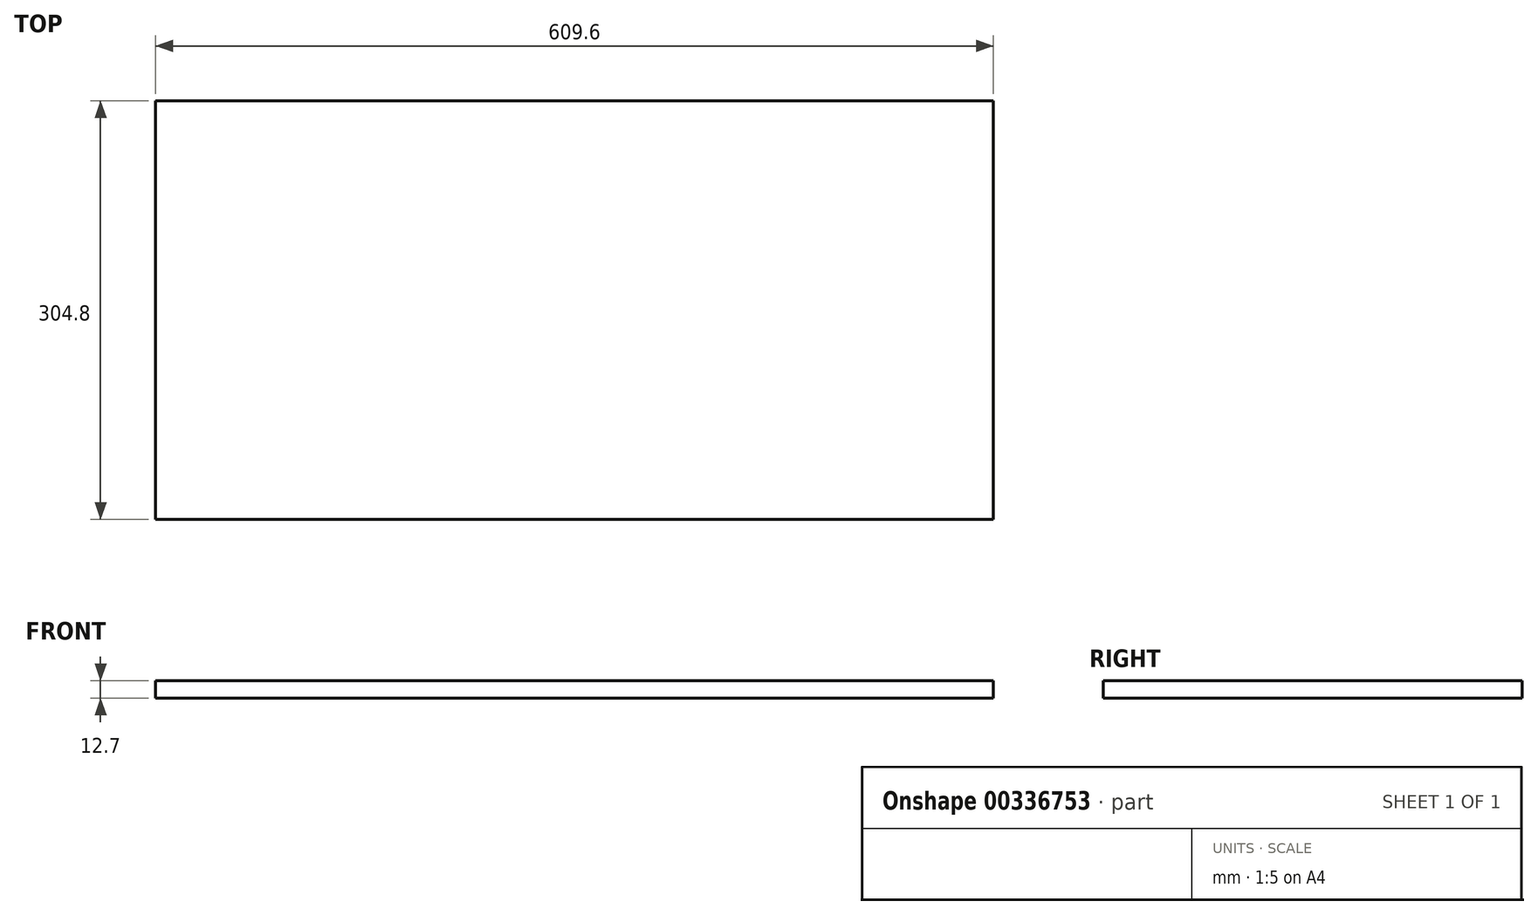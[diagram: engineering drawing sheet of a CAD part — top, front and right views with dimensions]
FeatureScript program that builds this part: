
annotation { "Feature Type Name" : "Feature", "Feature Type Description" : "" }
export const myFeature = defineFeature(function(context is Context, id is Id, definition is map)
    precondition{}
    {
        {
            var Q0;
            Q0=qCreatedBy(makeId("Top.planeOp"),FACE);
            var sketch = newSketch(context, id + "F0", { "sketchPlane" : qUnion([Q0])});
            skLineSegment(sketch, "E0.bottom", {"start": v(0, 0) * mm, "end": v(609.6, 0) * mm});
            skLineSegment(sketch, "E0.top", {"start": v(0, -304.8) * mm, "end": v(609.6, -304.8) * mm});
            skLineSegment(sketch, "E0.left", {"start": v(0, 0) * mm, "end": v(0, -304.8) * mm});
            skLineSegment(sketch, "E0.right", {"start": v(609.6, 0) * mm, "end": v(609.6, -304.8) * mm});
            skSolve(sketch);
        }
        {
            var Q0;
            Q0=makeQuery(id+"F0.imprint","IMPRINT",FACE,{"disambiguationData":[TD([[makeQuery(id+"F0.imprint","IMPRINT",EDGE,{"derivedFrom":sQuery(id+"F0.wireOp",EDGE,"E0.bottom")}),-1.0]])]});
            extrude(context, id + "F1", {"entities" : qUnion([Q0]), "depth" : 12.7 * mm});
        }
    });
